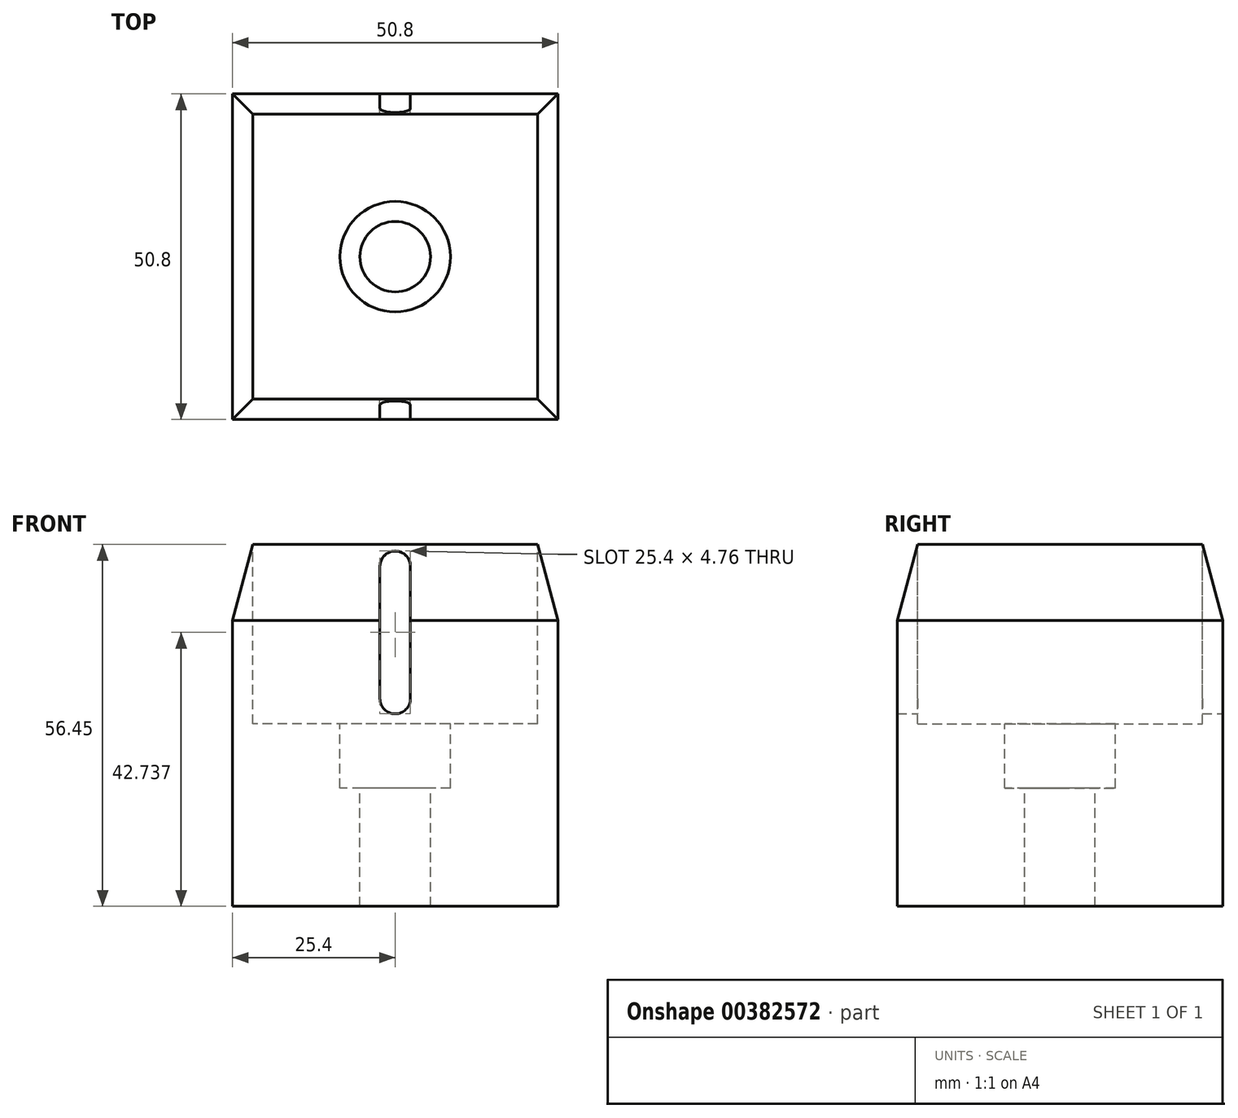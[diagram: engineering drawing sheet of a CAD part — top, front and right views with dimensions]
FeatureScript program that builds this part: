
annotation { "Feature Type Name" : "Feature", "Feature Type Description" : "" }
export const myFeature = defineFeature(function(context is Context, id is Id, definition is map)
    precondition{}
    {
        {
            var Q0;
            Q0=qCreatedBy(makeId("Top.planeOp"),FACE);
            var sketch = newSketch(context, id + "F0", { "sketchPlane" : qUnion([Q0])});
            skLineSegment(sketch, "E0.bottom", {"start": v(25.4, -25.4) * mm, "end": v(-25.4, -25.4) * mm});
            skLineSegment(sketch, "E0.top", {"start": v(25.4, 25.4) * mm, "end": v(-25.4, 25.4) * mm});
            skLineSegment(sketch, "E0.left", {"start": v(25.4, -25.4) * mm, "end": v(25.4, 25.4) * mm});
            skLineSegment(sketch, "E0.right", {"start": v(-25.4, -25.4) * mm, "end": v(-25.4, 25.4) * mm});
            skPoint(sketch, "E0.middle", {"position": v(0, 0) * mm});
            skSolve(sketch);
        }
        {
            var Q0;
            Q0 = qSketchRegion(id + "F0", true);
            extrude(context, id + "F1", {"entities" : qUnion([Q0]), "depth" : 56.45 * mm});
        }
        {
            var Q0;
            Q0=makeQuery(id+"F1.opExtrude","CAP_FACE",FACE,{"disambiguationData":[OSD([sQuery(id+"F0.wireOp",EDGE,"E0.bottom"),sQuery(id+"F0.wireOp",EDGE,"E0.top"),sQuery(id+"F0.wireOp",EDGE,"E0.left"),sQuery(id+"F0.wireOp",EDGE,"E0.right")])],"isStart":false});
            var sketch = newSketch(context, id + "F2", { "sketchPlane" : qUnion([Q0])});
            skLineSegment(sketch, "E1.bottom", {"start": v(22.23, -22.23) * mm, "end": v(-22.23, -22.23) * mm});
            skLineSegment(sketch, "E1.top", {"start": v(22.23, 22.23) * mm, "end": v(-22.23, 22.23) * mm});
            skLineSegment(sketch, "E1.left", {"start": v(22.23, -22.23) * mm, "end": v(22.23, 22.23) * mm});
            skLineSegment(sketch, "E1.right", {"start": v(-22.23, -22.23) * mm, "end": v(-22.23, 22.23) * mm});
            skPoint(sketch, "E1.middle", {"position": v(0, 0) * mm});
            skSolve(sketch);
        }
        {
            var Q0;
            Q0 = qSketchRegion(id + "F2", true);
            extrude(context, id + "F3", {"entities" : qUnion([Q0]), "operationType" : NewBodyOperationType.REMOVE, "oppositeDirection" : true, "depth" : 28 * mm});
        }
        {
            var Q0;
            Q0=makeQuery(id+"F3.boolean.opBoolean","COPY",FACE,{"derivedFrom":makeQuery(id+"F3.opExtrude","CAP_FACE",FACE,{"disambiguationData":[OSD([sQuery(id+"F2.wireOp",EDGE,"E1.bottom"),sQuery(id+"F2.wireOp",EDGE,"E1.top"),sQuery(id+"F2.wireOp",EDGE,"E1.left"),sQuery(id+"F2.wireOp",EDGE,"E1.right")])],"isStart":false})});
            var sketch = newSketch(context, id + "F4", { "sketchPlane" : qUnion([Q0])});
            skPoint(sketch, "E2", {"position": v(0, 0) * mm});
            skSolve(sketch);
        }
        {
            var Q0;
            Q0=sQuery(id+"F4.wireOp",VERTEX,"E2");
            var Q1;
            Q1=makeQuery(id+"F1.opExtrude","SWEPT_BODY",BODY,{"disambiguationData":[OSD([sQuery(id+"F0.wireOp",EDGE,"E0.bottom"),sQuery(id+"F0.wireOp",EDGE,"E0.top"),sQuery(id+"F0.wireOp",EDGE,"E0.left"),sQuery(id+"F0.wireOp",EDGE,"E0.right")])]});
            hole(context, id + "F5", {"style" : HoleStyle.C_BORE, "endStyle" : HoleEndStyle.THROUGH, "standardTappedOrClearance" : lookupTablePath({ "standard" : "ISO", "fit" : "Normal", "size" : "M10", "type" : "Clearance" }), "standardBlindInLast" : lookupTablePath({ "fit" : "Standard", "standard" : "ISO", "size" : "M10", "type" : "Clearance" }), "holeDiameter" : 11 * mm, "cBoreDiameter" : 17.25 * mm, "cBoreDepth" : 10 * mm, "isTappedThrough" : true, "tappedDepth" : 12.7 * mm, "tapClearance" : 3, "locations" : qUnion([Q0]), "scope" : qUnion([Q1])});
        }
        {
            var Q0;
            Q0=makeQuery(id+"F1.opExtrude","CAP_EDGE",EDGE,{"disambiguationData":[OSD([sQuery(id+"F0.wireOp",EDGE,"E0.top")])],"isStart":false});
            var Q1;
            Q1=makeQuery(id+"F1.opExtrude","CAP_EDGE",EDGE,{"disambiguationData":[OSD([sQuery(id+"F0.wireOp",EDGE,"E0.left")])],"isStart":false});
            var Q2;
            Q2=makeQuery(id+"F1.opExtrude","CAP_EDGE",EDGE,{"disambiguationData":[OSD([sQuery(id+"F0.wireOp",EDGE,"E0.bottom")])],"isStart":false});
            var Q3;
            Q3=makeQuery(id+"F1.opExtrude","CAP_EDGE",EDGE,{"disambiguationData":[OSD([sQuery(id+"F0.wireOp",EDGE,"E0.right")])],"isStart":false});
            chamfer(context, id + "F6", {"entities" : qUnion([Q0, Q1, Q2, Q3]), "chamferType" : ChamferType.OFFSET_ANGLE, "width" : 3.17 * mm, "oppositeDirection" : false, "angle" : 75 * degree, "tangentPropagation" : true});
        }
        {
            var Q0;
            Q0=makeQuery(id+"F1.opExtrude","SWEPT_FACE",FACE,{"disambiguationData":[OSD([sQuery(id+"F0.wireOp",EDGE,"E0.top")])]});
            cPlane(context, id + "F7", {"entities" : qUnion([Q0]), "cplaneType" : CPlaneType.OFFSET, "offset" : 0 * mm, "width" : 152.4 * mm, "height" : 152.4 * mm});
        }
        {
            var Q0;
            Q0=qCreatedBy(id+"F7.planeOp",FACE);
            var sketch = newSketch(context, id + "F8", { "sketchPlane" : qUnion([Q0])});
            skLineSegment(sketch, "E3", {"start": v(0, 71.95) * mm, "end": v(0, 0) * mm, "construction": true});
            skLineSegment(sketch, "E4.bottom", {"start": v(2.38, 32.42) * mm, "end": v(-2.38, 32.42) * mm});
            skLineSegment(sketch, "E4.top", {"start": v(2.38, 53.06) * mm, "end": v(-2.38, 53.06) * mm});
            skLineSegment(sketch, "E4.left", {"start": v(2.38, 32.42) * mm, "end": v(2.38, 53.06) * mm});
            skLineSegment(sketch, "E4.right", {"start": v(-2.38, 32.42) * mm, "end": v(-2.38, 53.06) * mm});
            skPoint(sketch, "E4.middle", {"position": v(0, 42.74) * mm});
            skArc(sketch, "E5", {"start": v(-2.38, 53.06) * mm, "mid": v(0, 55.44) * mm, "end": v(2.38, 53.06) * mm});
            skArc(sketch, "E6", {"start": v(-2.38, 32.42) * mm, "mid": v(0, 30.04) * mm, "end": v(2.38, 32.42) * mm});
            skSolve(sketch);
        }
        {
            var Q0;
            Q0 = qSketchRegion(id + "F8", true);
            extrude(context, id + "F9", {"entities" : qUnion([Q0]), "operationType" : NewBodyOperationType.REMOVE, "endBound" : BoundingType.THROUGH_ALL, "oppositeDirection" : true, "depth" : 25.4 * mm});
        }
    });
